# Revit family: Electric_Furnace-Unico-Square_Plenum NEW
name_source: partatom
category: Mechanical Equipment
units: mm (PartAtom-declared; Revit-internal decimal feet)

## family parameters
Always vertical = Yes
Classification = None
Cut with Voids When Loaded = No
OmniClass Number = 23.75.70.00
OmniClass Title = HVAC Distribution Devices
Part Type = Normal
Room Calculation Point = No
Round Connector Dimension = Use Diameter
Shared = No
Work Plane-Based = No

## types (1)
- Not a Type - Load Type Catalog
    Apparent Load = 8 VA
    Assembly Code = D3040100
    Constraints = 1
    Default Elevation = 0' - 0"
    Description = Electric Furnace
    Finish = Metal - Unico - Silver
    Frequency = 60 Hz
    Height = 1' - 0"
    Instruction Sheet Link = https://www.unicosystem.com
    Keynote = 23 30 00
    Length = 1' - 1"
    Load Classification = HVAC
    Manufacturer = Unico, Inc.
    Manufacturer Fax Number = 314-457-9000
    Model = WON0202-C
    Nominal Capacity = 2000 W
    Number of Poles = 1
    Performance URL = https://www.unicosystem.com
    Power Factor = 1
    Product Documentation Link = https://shop.unicosystem.com
    Product Page URL = https://shop.unicosystem.com
    URL = https://www.unicosystem.com
    Version = 2020 - v1.0a
    Video Link = https://www.youtube.com
    Warranty URL = https://www.unicosystem.com
    Width = 1' - 0"

## geometry (parser evidence)
native form markers: Sweep x5
no freeform markers — native parametric forms only
